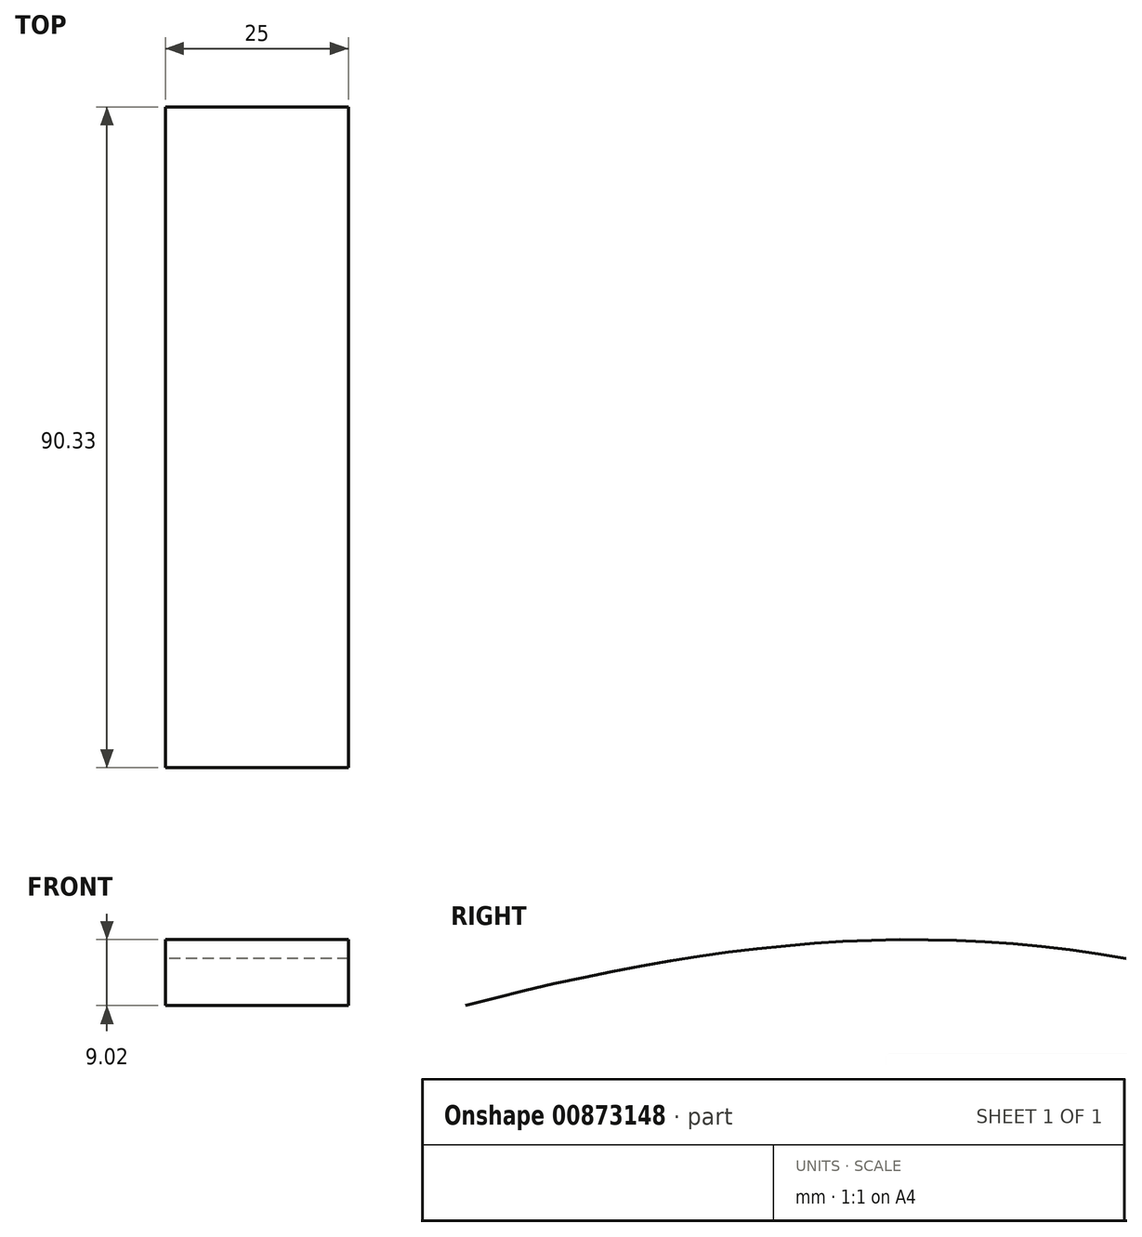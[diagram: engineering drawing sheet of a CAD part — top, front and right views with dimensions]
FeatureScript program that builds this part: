
annotation { "Feature Type Name" : "Feature", "Feature Type Description" : "" }
export const myFeature = defineFeature(function(context is Context, id is Id, definition is map)
    precondition{}
    {
        {
            var Q0;
            Q0=qCreatedBy(makeId("Right.planeOp"),FACE);
            var sketch = newSketch(context, id + "F0", { "sketchPlane" : qUnion([Q0])});
            skFitSpline(sketch, "E0", {"points": [v(-43.15, 8.1) * mm, v(47.18, 14.5) * mm], "startDerivative": vector(93.38, 24.72) * mm, "endDerivative": vector(88.8, -16.48) * mm});
            skSolve(sketch);
        }
        {
            var Q0;
            Q0=sQuery(id+"F0.wireOp",EDGE,"E0");
            extrude(context, id + "F1", {"bodyType" : ToolBodyType.SURFACE, "surfaceEntities" : qUnion([Q0]), "oppositeDirection" : true, "depth" : 25 * mm, "offsetDistance" : 25 * mm});
        }
    });
